# Revit family: Скамейка чугунная «Квартал»
name_source: partatom
category: Мебель
revit_build: Autodesk Revit 2017 (Build: 20160225_1515(x64)
units: mm (PartAtom-declared; Revit-internal decimal feet)

## family parameters
Всегда вертикально = Да
Заголовок OmniClass = General Furniture and Specialties
На основе рабочей плоскости = Нет
Номер OmniClass = 23.40.20.00
Общий = Нет
При загрузке вырезать с полостями = Нет
Точка расчета площади = Нет

## types (5) — shared parameters
ADSK_Код изделия = 7161
ADSK_Материал доски = <По категории>
ADSK_Материал опоры = <По категории>
ADSK_Материал фурнитуры = <По категории>
ADSK_Размер_Высота = 790 мм
ADSK_Размер_Высота сидения = 440 мм
ADSK_Размер_Высота спинки = 380 мм
ADSK_Размер_Ширина = 700 мм
ADSK_Размер_Ширина сидения = 410 мм
URL = https://hobbyka.ru
Изготовитель = ООО "Хоббика"

## per-type parameters (varying)
| type | ADSK_Размер_Длина | Длина доски | Стоимость |
| Скамейка чугунная «Квартал» 1.5м | 1500 мм | 1414 мм | 18144 $ |
| Скамейка чугунная «Квартал» 1,8м | 1800 мм | 1714 мм | 19505 $ |
| Скамейка чугунная «Квартал» 2,0 | 2000 мм | 1914 мм | 0 $ |
| Скамейка чугунная «Квартал» 3,0м | 3000 мм | 2914 мм | 0 $ |
| Скамейка чугунная «Квартал» Кресло | 600 мм | 514 мм | 17144 $ |

note: column(s) folded — value = type name in every type: ADSK_Наименование
